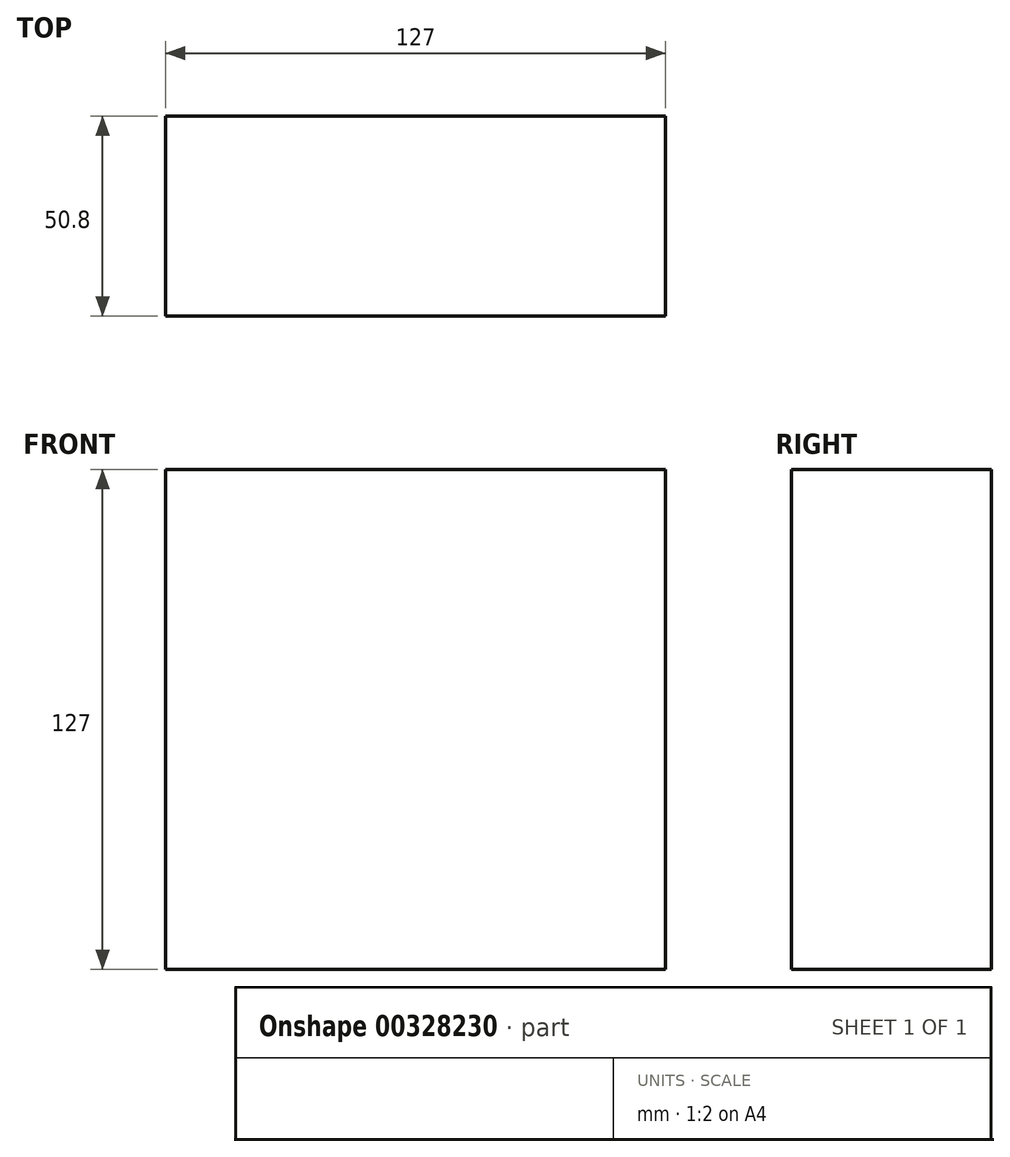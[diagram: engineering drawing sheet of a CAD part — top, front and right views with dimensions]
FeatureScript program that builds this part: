
annotation { "Feature Type Name" : "Feature", "Feature Type Description" : "" }
export const myFeature = defineFeature(function(context is Context, id is Id, definition is map)
    precondition{}
    {
        {
            var Q0;
            Q0=qCreatedBy(makeId("Front.planeOp"),FACE);
            var sketch = newSketch(context, id + "F0", { "sketchPlane" : qUnion([Q0])});
            skLineSegment(sketch, "E0", {"start": v(0, 0) * mm, "end": v(0, 127) * mm});
            skLineSegment(sketch, "E1", {"start": v(0, 127) * mm, "end": v(-127, 127) * mm});
            skLineSegment(sketch, "E2", {"start": v(-127, 127) * mm, "end": v(-127, 0) * mm});
            skLineSegment(sketch, "E3", {"start": v(-127, 0) * mm, "end": v(0, 0) * mm});
            skSolve(sketch);
        }
        {
            var Q0;
            Q0 = qSketchRegion(id + "F0", true);
            extrude(context, id + "F1", {"entities" : qUnion([Q0]), "depth" : 50.8 * mm});
        }
    });
